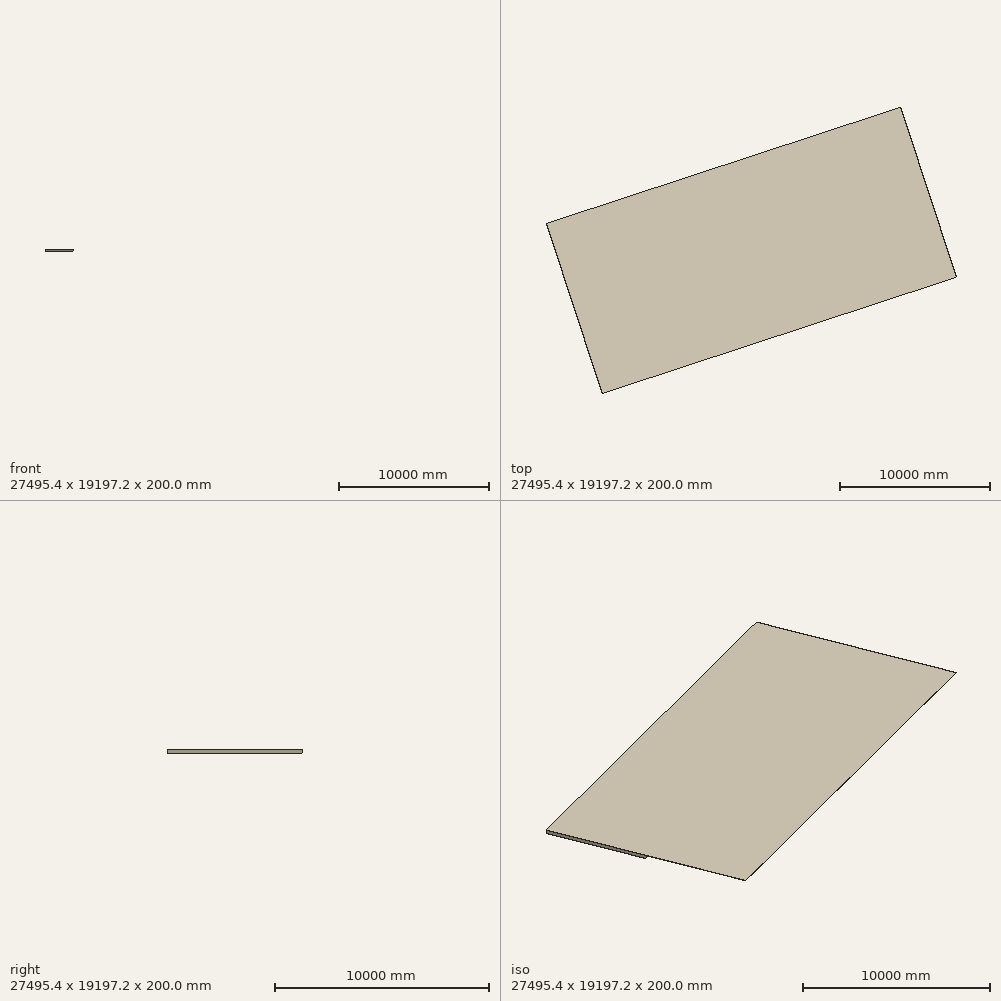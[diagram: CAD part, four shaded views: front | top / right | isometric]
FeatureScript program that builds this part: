
annotation { "Feature Type Name" : "Feature", "Feature Type Description" : "" }
export const myFeature = defineFeature(function(context is Context, id is Id, definition is map)
    precondition{}
    {
        {
            var Q0;
            Q0=qCreatedBy(makeId("Top.planeOp"),FACE);
            var sketch = newSketch(context, id + "F0", { "sketchPlane" : qUnion([Q0])});
            skLineSegment(sketch, "E0", {"start": v(0, 6314.85) * mm, "end": v(0, 0) * mm, "construction": true});
            skLineSegment(sketch, "E1.left", {"start": v(1870.93, -5700.85) * mm, "end": v(-1870.93, 5700.85) * mm});
            skLineSegment(sketch, "E2", {"start": v(-1870.93, 5700.85) * mm, "end": v(21882.6, 13496.37) * mm});
            skLineSegment(sketch, "E3", {"start": v(21882.6, 13496.37) * mm, "end": v(25624.45, 2094.68) * mm});
            skLineSegment(sketch, "E4", {"start": v(25624.45, 2094.68) * mm, "end": v(1870.93, -5700.85) * mm});
            skSolve(sketch);
        }
        {
            var Q0;
            Q0 = qSketchRegion(id + "F0", true);
            extrude(context, id + "F1", {"entities" : qUnion([Q0]), "depth" : 10 * mm, "offsetDistance" : 25 * mm});
        }
        {
            var Q0;
            Q0=makeQuery(id+"F1.opExtrude","CAP_FACE",FACE,{"disambiguationData":[OSD([sQuery(id+"F0.wireOp",EDGE,"E1.left"),sQuery(id+"F0.wireOp",EDGE,"E2"),sQuery(id+"F0.wireOp",EDGE,"E3"),sQuery(id+"F0.wireOp",EDGE,"E4")])],"isStart":true});
            var sketch = newSketch(context, id + "F2", { "sketchPlane" : qUnion([Q0])});
            skLineSegment(sketch, "E5", {"start": v(0, 0) * mm, "end": v(0, -6314.85) * mm});
            skSolve(sketch);
        }
        {
            var Q0;
            {var subQ0=sQuery(id+"F2.wireOp",EDGE,"E5");Q0=makeQuery(id+"F2.imprint","IMPRINT",FACE,{"disambiguationData":[TD([[makeQuery(id+"F2.imprint","IMPRINT",EDGE,{"derivedFrom":subQ0}),-1.0]])]});}
            extrude(context, id + "F3", {"entities" : qUnion([Q0]), "operationType" : NewBodyOperationType.ADD, "depth" : 190 * mm, "offsetDistance" : 25 * mm});
        }
    });
